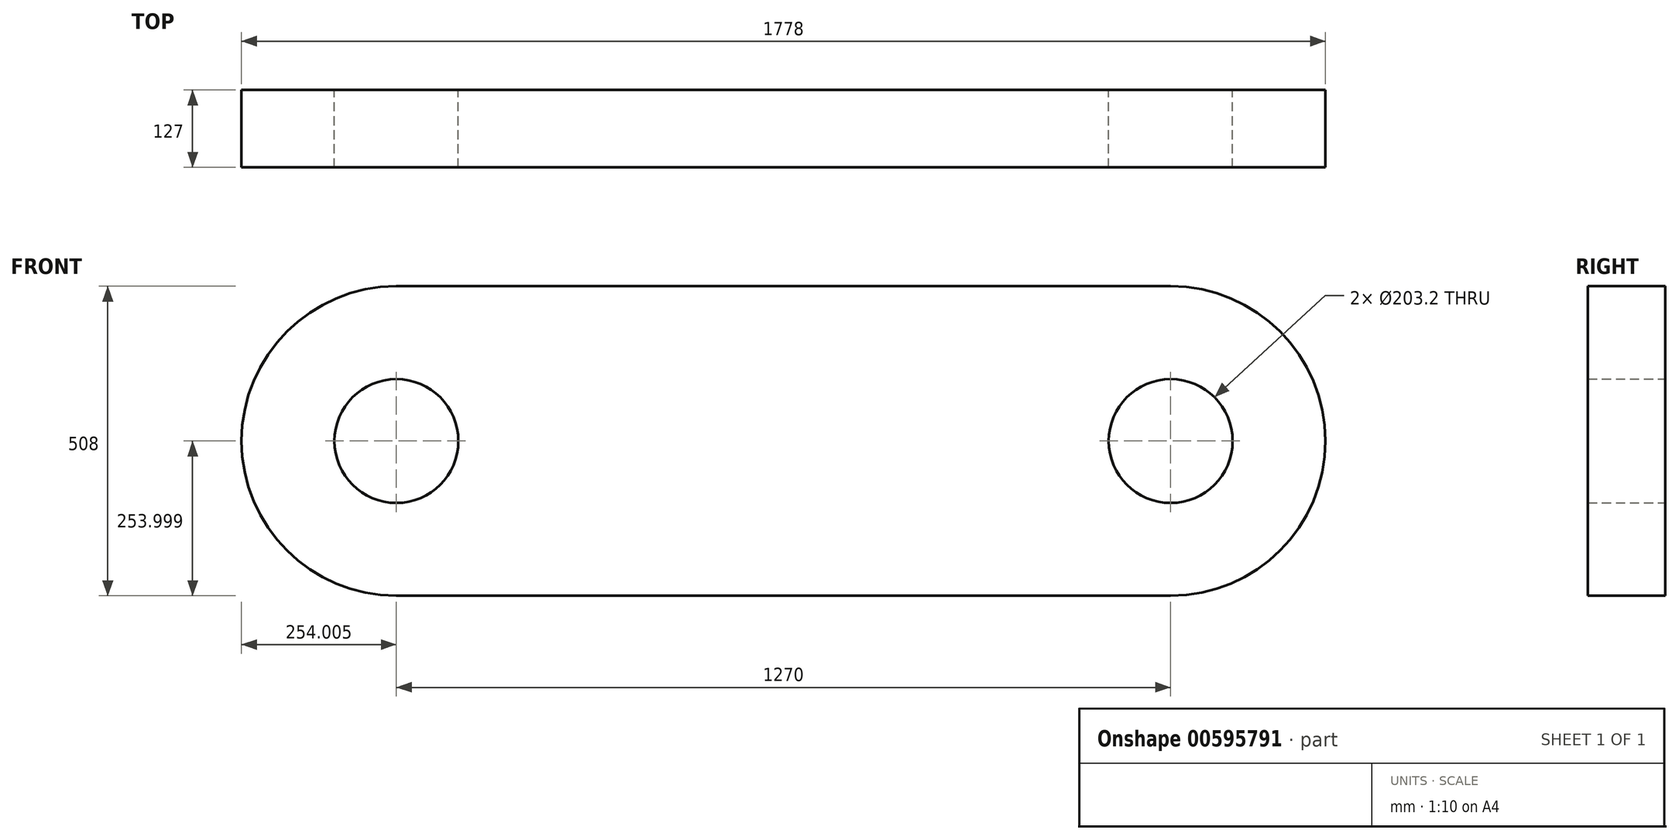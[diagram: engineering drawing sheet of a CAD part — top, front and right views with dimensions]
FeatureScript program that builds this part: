
annotation { "Feature Type Name" : "Feature", "Feature Type Description" : "" }
export const myFeature = defineFeature(function(context is Context, id is Id, definition is map)
    precondition{}
    {
        {
            var Q0;
            Q0=qCreatedBy(makeId("Front.planeOp"),FACE);
            var sketch = newSketch(context, id + "F0", { "sketchPlane" : qUnion([Q0])});
            skLineSegment(sketch, "E0.bottom", {"start": v(-53.3, 488.47) * mm, "end": v(1216.7, 488.47) * mm});
            skLineSegment(sketch, "E0.top", {"start": v(-53.3, -19.53) * mm, "end": v(1216.7, -19.53) * mm});
            skLineSegment(sketch, "E0.left", {"start": v(-53.3, 488.47) * mm, "end": v(-53.3, -19.53) * mm, "construction": true});
            skLineSegment(sketch, "E0.right", {"start": v(1216.7, 488.47) * mm, "end": v(1216.7, -19.53) * mm, "construction": true});
            skArc(sketch, "E1", {"start": v(-53.3, 488.47) * mm, "mid": v(-307.3, 234.47) * mm, "end": v(-53.3, -19.53) * mm});
            skArc(sketch, "E2", {"start": v(1216.7, -19.53) * mm, "mid": v(1470.7, 234.47) * mm, "end": v(1216.7, 488.47) * mm});
            skCircle(sketch, "E3", {"center": v(-53.3, 234.47) * mm, "radius": 101.6 * mm});
            skCircle(sketch, "E4", {"center": v(1216.7, 234.47) * mm, "radius": 101.6 * mm});
            skSolve(sketch);
        }
        {
            var Q0;
            Q0=makeQuery(id+"F0.imprint","IMPRINT",FACE,{"disambiguationData":[TD([[makeQuery(id+"F0.imprint","IMPRINT",EDGE,{"derivedFrom":sQuery(id+"F0.wireOp",EDGE,"E0.bottom")}),-1.0]])]});
            extrude(context, id + "F1", {"entities" : qUnion([Q0]), "depth" : 127 * mm, "offsetDistance" : 25.4 * mm});
        }
    });
